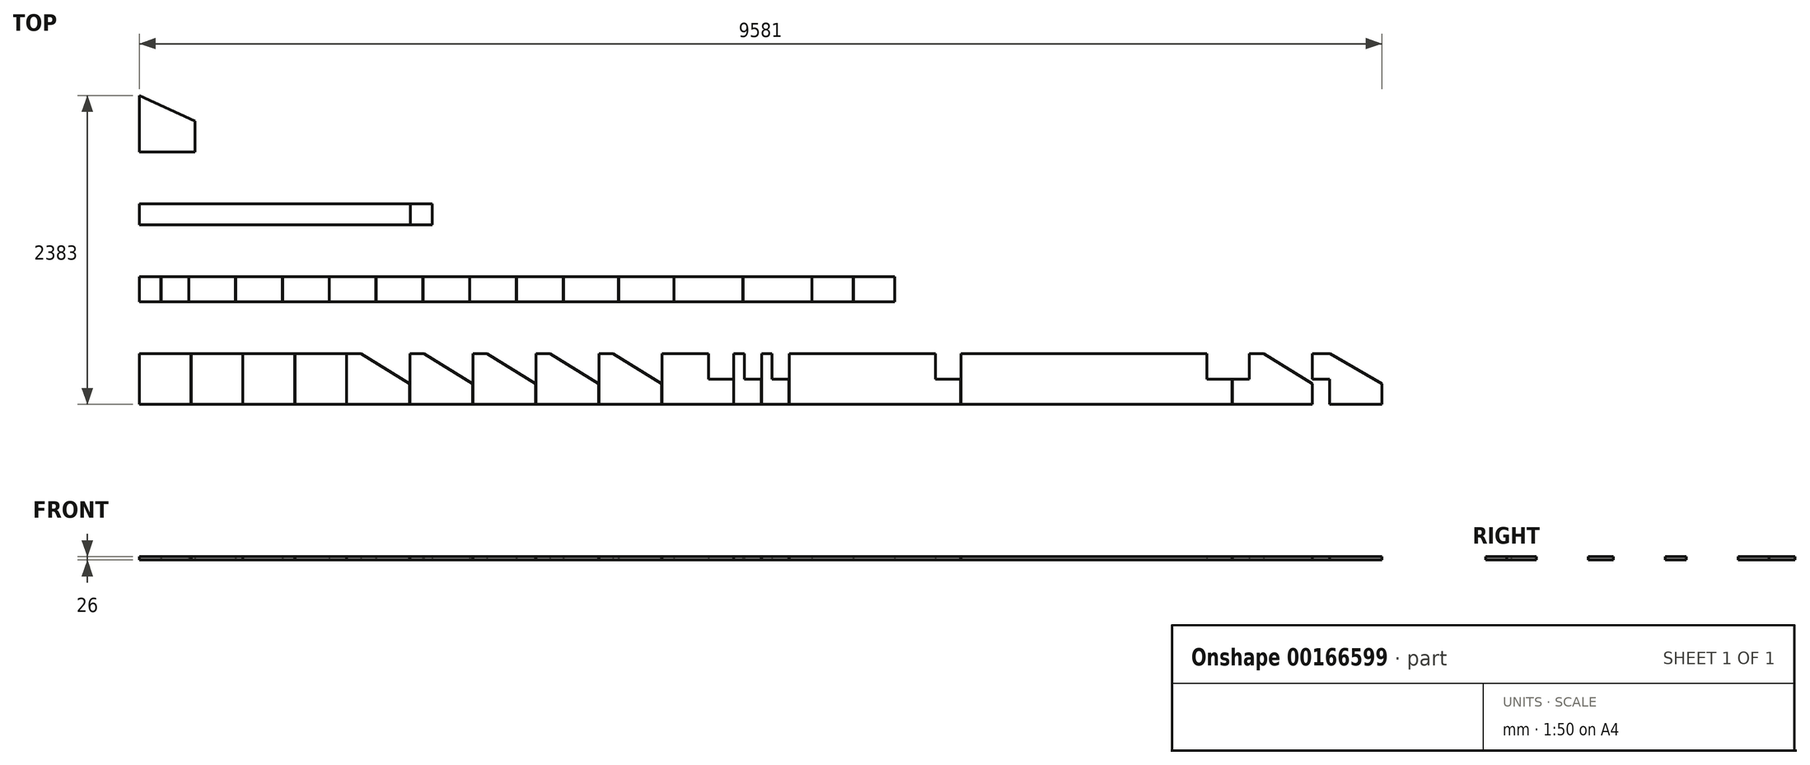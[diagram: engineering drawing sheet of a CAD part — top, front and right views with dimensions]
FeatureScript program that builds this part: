
annotation { "Feature Type Name" : "Feature", "Feature Type Description" : "" }
export const myFeature = defineFeature(function(context is Context, id is Id, definition is map)
    precondition{}
    {
        {
            var Q0;
            Q0=qCreatedBy(makeId("Top.planeOp"),FACE);
            var sketch = newSketch(context, id + "F0", { "sketchPlane" : qUnion([Q0])});
            skLineSegment(sketch, "E0.bottom", {"start": v(0, 0) * mm, "end": v(398, 0) * mm});
            skLineSegment(sketch, "E0.top", {"start": v(0, 390) * mm, "end": v(398, 390) * mm});
            skLineSegment(sketch, "E0.left", {"start": v(0, 0) * mm, "end": v(0, 390) * mm});
            skLineSegment(sketch, "E0.right", {"start": v(398, 0) * mm, "end": v(398, 390) * mm});
            skLineSegment(sketch, "E1.1.0.0", {"start": v(798, 0) * mm, "end": v(798, 390) * mm});
            skLineSegment(sketch, "E1.1.0.1", {"start": v(400, 0) * mm, "end": v(400, 390) * mm});
            skLineSegment(sketch, "E1.1.0.2", {"start": v(400, 390) * mm, "end": v(798, 390) * mm});
            skLineSegment(sketch, "E1.1.0.3", {"start": v(400, 0) * mm, "end": v(798, 0) * mm});
            skLineSegment(sketch, "E1.2.0.0", {"start": v(1198, 0) * mm, "end": v(1198, 390) * mm});
            skLineSegment(sketch, "E1.2.0.1", {"start": v(800, 0) * mm, "end": v(800, 390) * mm});
            skLineSegment(sketch, "E1.2.0.2", {"start": v(800, 390) * mm, "end": v(1198, 390) * mm});
            skLineSegment(sketch, "E1.2.0.3", {"start": v(800, 0) * mm, "end": v(1198, 0) * mm});
            skLineSegment(sketch, "E1.3.0.0", {"start": v(1598, 0) * mm, "end": v(1598, 390) * mm});
            skLineSegment(sketch, "E1.3.0.1", {"start": v(1200, 0) * mm, "end": v(1200, 390) * mm});
            skLineSegment(sketch, "E1.3.0.2", {"start": v(1200, 390) * mm, "end": v(1598, 390) * mm});
            skLineSegment(sketch, "E1.3.0.3", {"start": v(1200, 0) * mm, "end": v(1598, 0) * mm});
            skLineSegment(sketch, "E1.direction1", {"start": v(0, 0) * mm, "end": v(400, 0) * mm, "construction": true});
            skLineSegment(sketch, "E2.bottom", {"start": v(1600, 390) * mm, "end": v(1710, 390) * mm});
            skLineSegment(sketch, "E2.top", {"start": v(1600, 0) * mm, "end": v(2084, 0) * mm});
            skLineSegment(sketch, "E2.left", {"start": v(1600, 390) * mm, "end": v(1600, 0) * mm});
            skLineSegment(sketch, "E2.right", {"start": v(2084, 160) * mm, "end": v(2084, 0) * mm});
            skLineSegment(sketch, "E3", {"start": v(1710, 390) * mm, "end": v(2084, 160) * mm});
            skLineSegment(sketch, "E4.1.0.0", {"start": v(2086, 390) * mm, "end": v(2196, 390) * mm});
            skLineSegment(sketch, "E4.1.0.1", {"start": v(2196, 390) * mm, "end": v(2570, 160) * mm});
            skLineSegment(sketch, "E4.1.0.2", {"start": v(2086, 0) * mm, "end": v(2570, 0) * mm});
            skLineSegment(sketch, "E4.1.0.3", {"start": v(2570, 160) * mm, "end": v(2570, 0) * mm});
            skLineSegment(sketch, "E4.1.0.4", {"start": v(2086, 390) * mm, "end": v(2086, 0) * mm});
            skLineSegment(sketch, "E4.2.0.0", {"start": v(2572, 390) * mm, "end": v(2682, 390) * mm});
            skLineSegment(sketch, "E4.2.0.1", {"start": v(2682, 390) * mm, "end": v(3056, 160) * mm});
            skLineSegment(sketch, "E4.2.0.2", {"start": v(2572, 0) * mm, "end": v(3056, 0) * mm});
            skLineSegment(sketch, "E4.2.0.3", {"start": v(3056, 160) * mm, "end": v(3056, 0) * mm});
            skLineSegment(sketch, "E4.2.0.4", {"start": v(2572, 390) * mm, "end": v(2572, 0) * mm});
            skLineSegment(sketch, "E4.3.0.0", {"start": v(3058, 390) * mm, "end": v(3168, 390) * mm});
            skLineSegment(sketch, "E4.3.0.1", {"start": v(3168, 390) * mm, "end": v(3542, 160) * mm});
            skLineSegment(sketch, "E4.3.0.2", {"start": v(3058, 0) * mm, "end": v(3542, 0) * mm});
            skLineSegment(sketch, "E4.3.0.3", {"start": v(3542, 160) * mm, "end": v(3542, 0) * mm});
            skLineSegment(sketch, "E4.3.0.4", {"start": v(3058, 390) * mm, "end": v(3058, 0) * mm});
            skLineSegment(sketch, "E4.4.0.0", {"start": v(3544, 390) * mm, "end": v(3654, 390) * mm});
            skLineSegment(sketch, "E4.4.0.1", {"start": v(3654, 390) * mm, "end": v(4028, 160) * mm});
            skLineSegment(sketch, "E4.4.0.2", {"start": v(3544, 0) * mm, "end": v(4028, 0) * mm});
            skLineSegment(sketch, "E4.4.0.3", {"start": v(4028, 160) * mm, "end": v(4028, 0) * mm});
            skLineSegment(sketch, "E4.4.0.4", {"start": v(3544, 390) * mm, "end": v(3544, 0) * mm});
            skLineSegment(sketch, "E4.direction1", {"start": v(1600, 0) * mm, "end": v(2086, 0) * mm, "construction": true});
            skLineSegment(sketch, "E5.bottom", {"start": v(0, 790) * mm, "end": v(167, 790) * mm});
            skLineSegment(sketch, "E5.top", {"start": v(0, 985) * mm, "end": v(167, 985) * mm});
            skLineSegment(sketch, "E5.left", {"start": v(0, 790) * mm, "end": v(0, 985) * mm});
            skLineSegment(sketch, "E5.right", {"start": v(167, 790) * mm, "end": v(167, 985) * mm});
            skLineSegment(sketch, "E6.bottom", {"start": v(169, 790) * mm, "end": v(381, 790) * mm});
            skLineSegment(sketch, "E6.top", {"start": v(169, 985) * mm, "end": v(381, 985) * mm});
            skLineSegment(sketch, "E6.left", {"start": v(169, 790) * mm, "end": v(169, 985) * mm});
            skLineSegment(sketch, "E6.right", {"start": v(381, 790) * mm, "end": v(381, 985) * mm});
            skLineSegment(sketch, "E7.bottom", {"start": v(383, 790) * mm, "end": v(742, 790) * mm});
            skLineSegment(sketch, "E7.top", {"start": v(383, 985) * mm, "end": v(742, 985) * mm});
            skLineSegment(sketch, "E7.left", {"start": v(383, 790) * mm, "end": v(383, 985) * mm});
            skLineSegment(sketch, "E7.right", {"start": v(742, 790) * mm, "end": v(742, 985) * mm});
            skLineSegment(sketch, "E8.1.0.0", {"start": v(744, 985) * mm, "end": v(1103, 985) * mm});
            skLineSegment(sketch, "E8.1.0.1", {"start": v(744, 790) * mm, "end": v(744, 985) * mm});
            skLineSegment(sketch, "E8.1.0.2", {"start": v(744, 790) * mm, "end": v(1103, 790) * mm});
            skLineSegment(sketch, "E8.1.0.3", {"start": v(1103, 790) * mm, "end": v(1103, 985) * mm});
            skLineSegment(sketch, "E8.2.0.0", {"start": v(1105, 985) * mm, "end": v(1464, 985) * mm});
            skLineSegment(sketch, "E8.2.0.1", {"start": v(1105, 790) * mm, "end": v(1105, 985) * mm});
            skLineSegment(sketch, "E8.2.0.2", {"start": v(1105, 790) * mm, "end": v(1464, 790) * mm});
            skLineSegment(sketch, "E8.2.0.3", {"start": v(1464, 790) * mm, "end": v(1464, 985) * mm});
            skLineSegment(sketch, "E8.3.0.0", {"start": v(1466, 985) * mm, "end": v(1825, 985) * mm});
            skLineSegment(sketch, "E8.3.0.1", {"start": v(1466, 790) * mm, "end": v(1466, 985) * mm});
            skLineSegment(sketch, "E8.3.0.2", {"start": v(1466, 790) * mm, "end": v(1825, 790) * mm});
            skLineSegment(sketch, "E8.3.0.3", {"start": v(1825, 790) * mm, "end": v(1825, 985) * mm});
            skLineSegment(sketch, "E8.4.0.0", {"start": v(1827, 985) * mm, "end": v(2186, 985) * mm});
            skLineSegment(sketch, "E8.4.0.1", {"start": v(1827, 790) * mm, "end": v(1827, 985) * mm});
            skLineSegment(sketch, "E8.4.0.2", {"start": v(1827, 790) * mm, "end": v(2186, 790) * mm});
            skLineSegment(sketch, "E8.4.0.3", {"start": v(2186, 790) * mm, "end": v(2186, 985) * mm});
            skLineSegment(sketch, "E8.5.0.0", {"start": v(2188, 985) * mm, "end": v(2547, 985) * mm});
            skLineSegment(sketch, "E8.5.0.1", {"start": v(2188, 790) * mm, "end": v(2188, 985) * mm});
            skLineSegment(sketch, "E8.5.0.2", {"start": v(2188, 790) * mm, "end": v(2547, 790) * mm});
            skLineSegment(sketch, "E8.5.0.3", {"start": v(2547, 790) * mm, "end": v(2547, 985) * mm});
            skLineSegment(sketch, "E8.6.0.0", {"start": v(2549, 985) * mm, "end": v(2908, 985) * mm});
            skLineSegment(sketch, "E8.6.0.1", {"start": v(2549, 790) * mm, "end": v(2549, 985) * mm});
            skLineSegment(sketch, "E8.6.0.2", {"start": v(2549, 790) * mm, "end": v(2908, 790) * mm});
            skLineSegment(sketch, "E8.6.0.3", {"start": v(2908, 790) * mm, "end": v(2908, 985) * mm});
            skLineSegment(sketch, "E8.7.0.0", {"start": v(2910, 985) * mm, "end": v(3269, 985) * mm});
            skLineSegment(sketch, "E8.7.0.1", {"start": v(2910, 790) * mm, "end": v(2910, 985) * mm});
            skLineSegment(sketch, "E8.7.0.2", {"start": v(2910, 790) * mm, "end": v(3269, 790) * mm});
            skLineSegment(sketch, "E8.7.0.3", {"start": v(3269, 790) * mm, "end": v(3269, 985) * mm});
            skLineSegment(sketch, "E8.direction1", {"start": v(383, 790) * mm, "end": v(744, 790) * mm, "construction": true});
            skLineSegment(sketch, "E9.bottom", {"start": v(3271, 790) * mm, "end": v(3695, 790) * mm});
            skLineSegment(sketch, "E9.top", {"start": v(3271, 985) * mm, "end": v(3695, 985) * mm});
            skLineSegment(sketch, "E9.left", {"start": v(3271, 790) * mm, "end": v(3271, 985) * mm});
            skLineSegment(sketch, "E9.right", {"start": v(3695, 790) * mm, "end": v(3695, 985) * mm});
            skLineSegment(sketch, "E10.1.0.0", {"start": v(4121, 790) * mm, "end": v(4121, 985) * mm});
            skLineSegment(sketch, "E10.1.0.1", {"start": v(3697, 790) * mm, "end": v(3697, 985) * mm});
            skLineSegment(sketch, "E10.1.0.2", {"start": v(3697, 985) * mm, "end": v(4121, 985) * mm});
            skLineSegment(sketch, "E10.1.0.3", {"start": v(3697, 790) * mm, "end": v(4121, 790) * mm});
            skLineSegment(sketch, "E10.direction1", {"start": v(3271, 790) * mm, "end": v(3697, 790) * mm, "construction": true});
            skLineSegment(sketch, "E11.bottom", {"start": v(4123, 790) * mm, "end": v(4653, 790) * mm});
            skLineSegment(sketch, "E11.top", {"start": v(4123, 985) * mm, "end": v(4653, 985) * mm});
            skLineSegment(sketch, "E11.left", {"start": v(4123, 790) * mm, "end": v(4123, 985) * mm});
            skLineSegment(sketch, "E11.right", {"start": v(4653, 790) * mm, "end": v(4653, 985) * mm});
            skLineSegment(sketch, "E12.1.0.0", {"start": v(4655, 790) * mm, "end": v(4655, 985) * mm});
            skLineSegment(sketch, "E12.1.0.1", {"start": v(4655, 790) * mm, "end": v(5185, 790) * mm});
            skLineSegment(sketch, "E12.1.0.2", {"start": v(4655, 985) * mm, "end": v(5185, 985) * mm});
            skLineSegment(sketch, "E12.1.0.3", {"start": v(5185, 790) * mm, "end": v(5185, 985) * mm});
            skLineSegment(sketch, "E12.direction1", {"start": v(4123, 790) * mm, "end": v(4655, 790) * mm, "construction": true});
            skLineSegment(sketch, "E13.bottom", {"start": v(5187, 790) * mm, "end": v(5505, 790) * mm});
            skLineSegment(sketch, "E13.top", {"start": v(5187, 985) * mm, "end": v(5505, 985) * mm});
            skLineSegment(sketch, "E13.left", {"start": v(5187, 790) * mm, "end": v(5187, 985) * mm});
            skLineSegment(sketch, "E13.right", {"start": v(5505, 790) * mm, "end": v(5505, 985) * mm});
            skLineSegment(sketch, "E14.1.0.0", {"start": v(5507, 790) * mm, "end": v(5825, 790) * mm});
            skLineSegment(sketch, "E14.1.0.1", {"start": v(5507, 985) * mm, "end": v(5825, 985) * mm});
            skLineSegment(sketch, "E14.1.0.2", {"start": v(5507, 790) * mm, "end": v(5507, 985) * mm});
            skLineSegment(sketch, "E14.1.0.3", {"start": v(5825, 790) * mm, "end": v(5825, 985) * mm});
            skLineSegment(sketch, "E14.direction1", {"start": v(5187, 790) * mm, "end": v(5507, 790) * mm, "construction": true});
            skLineSegment(sketch, "E15.bottom", {"start": v(4030, 0) * mm, "end": v(4582, 0) * mm});
            skLineSegment(sketch, "E15.top", {"start": v(4030, 390) * mm, "end": v(4389, 390) * mm});
            skLineSegment(sketch, "E15.left", {"start": v(4030, 0) * mm, "end": v(4030, 390) * mm});
            skLineSegment(sketch, "E15.right", {"start": v(4582, 0) * mm, "end": v(4582, 195) * mm});
            skLineSegment(sketch, "E16", {"start": v(4389, 390) * mm, "end": v(4389, 195) * mm});
            skLineSegment(sketch, "E17", {"start": v(4389, 195) * mm, "end": v(4582, 195) * mm});
            skLineSegment(sketch, "E18.bottom", {"start": v(4584, 0) * mm, "end": v(4796, 0) * mm});
            skLineSegment(sketch, "E18.top", {"start": v(4584, 390) * mm, "end": v(4664, 390) * mm});
            skLineSegment(sketch, "E18.left", {"start": v(4584, 0) * mm, "end": v(4584, 390) * mm});
            skLineSegment(sketch, "E18.right", {"start": v(4796, 0) * mm, "end": v(4796, 195) * mm});
            skLineSegment(sketch, "E19", {"start": v(4664, 390) * mm, "end": v(4664, 195) * mm});
            skLineSegment(sketch, "E20", {"start": v(4664, 195) * mm, "end": v(4796, 195) * mm});
            skLineSegment(sketch, "E21.1.0.0", {"start": v(4798, 390) * mm, "end": v(4878, 390) * mm});
            skLineSegment(sketch, "E21.1.0.1", {"start": v(4798, 0) * mm, "end": v(5010, 0) * mm});
            skLineSegment(sketch, "E21.1.0.2", {"start": v(4878, 390) * mm, "end": v(4878, 195) * mm});
            skLineSegment(sketch, "E21.1.0.3", {"start": v(5010, 0) * mm, "end": v(5010, 195) * mm});
            skLineSegment(sketch, "E21.1.0.4", {"start": v(4798, 0) * mm, "end": v(4798, 390) * mm});
            skLineSegment(sketch, "E21.1.0.5", {"start": v(4878, 195) * mm, "end": v(5010, 195) * mm});
            skLineSegment(sketch, "E21.direction1", {"start": v(4584, 0) * mm, "end": v(4798, 0) * mm, "construction": true});
            skLineSegment(sketch, "E22.bottom", {"start": v(5012, 0) * mm, "end": v(6333, 0) * mm});
            skLineSegment(sketch, "E22.top", {"start": v(5012, 390) * mm, "end": v(6140, 390) * mm});
            skLineSegment(sketch, "E22.left", {"start": v(5012, 0) * mm, "end": v(5012, 390) * mm});
            skLineSegment(sketch, "E22.right", {"start": v(6333, 0) * mm, "end": v(6333, 195) * mm});
            skLineSegment(sketch, "E23", {"start": v(6140, 390) * mm, "end": v(6140, 195) * mm});
            skLineSegment(sketch, "E24", {"start": v(6140, 195) * mm, "end": v(6333, 195) * mm});
            skLineSegment(sketch, "E25.bottom", {"start": v(6335, 0) * mm, "end": v(8425, 0) * mm});
            skLineSegment(sketch, "E25.top", {"start": v(6335, 390) * mm, "end": v(8232, 390) * mm});
            skLineSegment(sketch, "E25.left", {"start": v(6335, 0) * mm, "end": v(6335, 390) * mm});
            skLineSegment(sketch, "E25.right", {"start": v(8425, 0) * mm, "end": v(8425, 195) * mm});
            skLineSegment(sketch, "E26", {"start": v(8232, 390) * mm, "end": v(8232, 195) * mm});
            skLineSegment(sketch, "E27", {"start": v(8232, 195) * mm, "end": v(8425, 195) * mm});
            skLineSegment(sketch, "E28.bottom", {"start": v(0, 1385) * mm, "end": v(2090, 1385) * mm});
            skLineSegment(sketch, "E28.top", {"start": v(0, 1545) * mm, "end": v(2090, 1545) * mm});
            skLineSegment(sketch, "E28.left", {"start": v(0, 1385) * mm, "end": v(0, 1545) * mm});
            skLineSegment(sketch, "E28.right", {"start": v(2090, 1385) * mm, "end": v(2090, 1545) * mm});
            skLineSegment(sketch, "E29.bottom", {"start": v(8427, 0) * mm, "end": v(9043, 0) * mm});
            skLineSegment(sketch, "E29.top", {"start": v(8559, 390) * mm, "end": v(8669, 390) * mm});
            skLineSegment(sketch, "E29.left", {"start": v(8427, 0) * mm, "end": v(8427, 195) * mm});
            skLineSegment(sketch, "E29.right", {"start": v(9043, 0) * mm, "end": v(9043, 160) * mm});
            skLineSegment(sketch, "E30", {"start": v(8559, 390) * mm, "end": v(8559, 195) * mm});
            skLineSegment(sketch, "E31", {"start": v(8559, 195) * mm, "end": v(8427, 195) * mm});
            skLineSegment(sketch, "E32", {"start": v(8669, 390) * mm, "end": v(9043, 160) * mm});
            skLineSegment(sketch, "E33.bottom", {"start": v(9177, 0) * mm, "end": v(9581, 0) * mm});
            skLineSegment(sketch, "E33.top", {"start": v(9045, 390) * mm, "end": v(9181, 390) * mm});
            skLineSegment(sketch, "E33.left", {"start": v(9045, 195) * mm, "end": v(9045, 390) * mm});
            skLineSegment(sketch, "E33.right", {"start": v(9581, 0) * mm, "end": v(9581, 160) * mm});
            skLineSegment(sketch, "E34", {"start": v(9177, 0) * mm, "end": v(9177, 195) * mm});
            skLineSegment(sketch, "E35", {"start": v(9177, 195) * mm, "end": v(9045, 195) * mm});
            skLineSegment(sketch, "E36", {"start": v(9181, 390) * mm, "end": v(9581, 160) * mm});
            skLineSegment(sketch, "E37.bottom", {"start": v(0, 1945) * mm, "end": v(430, 1945) * mm});
            skLineSegment(sketch, "E37.left", {"start": v(0, 1945) * mm, "end": v(0, 2383) * mm});
            skLineSegment(sketch, "E37.right", {"start": v(430, 1945) * mm, "end": v(430, 2184) * mm});
            skLineSegment(sketch, "E38", {"start": v(0, 2383) * mm, "end": v(430, 2184) * mm});
            skLineSegment(sketch, "E39.bottom", {"start": v(2092, 1545) * mm, "end": v(2259, 1545) * mm});
            skLineSegment(sketch, "E39.top", {"start": v(2092, 1385) * mm, "end": v(2259, 1385) * mm});
            skLineSegment(sketch, "E39.left", {"start": v(2092, 1545) * mm, "end": v(2092, 1385) * mm});
            skLineSegment(sketch, "E39.right", {"start": v(2259, 1545) * mm, "end": v(2259, 1385) * mm});
            skLineSegment(sketch, "E40.bottom", {"start": v(0, -315.86) * mm, "end": v(2200, -315.86) * mm});
            skLineSegment(sketch, "E40.top", {"start": v(0, -905.86) * mm, "end": v(2200, -905.86) * mm});
            skLineSegment(sketch, "E40.left", {"start": v(0, -315.86) * mm, "end": v(0, -905.86) * mm});
            skLineSegment(sketch, "E40.right", {"start": v(2200, -315.86) * mm, "end": v(2200, -905.86) * mm});
            skLineSegment(sketch, "E41.1.0.0", {"start": v(2250, -905.86) * mm, "end": v(4450, -905.86) * mm});
            skLineSegment(sketch, "E41.1.0.1", {"start": v(4450, -315.86) * mm, "end": v(4450, -905.86) * mm});
            skLineSegment(sketch, "E41.1.0.2", {"start": v(2250, -315.86) * mm, "end": v(2250, -905.86) * mm});
            skLineSegment(sketch, "E41.1.0.3", {"start": v(2250, -315.86) * mm, "end": v(4450, -315.86) * mm});
            skLineSegment(sketch, "E41.2.0.0", {"start": v(4500, -905.86) * mm, "end": v(6700, -905.86) * mm});
            skLineSegment(sketch, "E41.2.0.1", {"start": v(6700, -315.86) * mm, "end": v(6700, -905.86) * mm});
            skLineSegment(sketch, "E41.2.0.2", {"start": v(4500, -315.86) * mm, "end": v(4500, -905.86) * mm});
            skLineSegment(sketch, "E41.2.0.3", {"start": v(4500, -315.86) * mm, "end": v(6700, -315.86) * mm});
            skLineSegment(sketch, "E41.3.0.0", {"start": v(6750, -905.86) * mm, "end": v(8950, -905.86) * mm});
            skLineSegment(sketch, "E41.3.0.1", {"start": v(8950, -315.86) * mm, "end": v(8950, -905.86) * mm});
            skLineSegment(sketch, "E41.3.0.2", {"start": v(6750, -315.86) * mm, "end": v(6750, -905.86) * mm});
            skLineSegment(sketch, "E41.3.0.3", {"start": v(6750, -315.86) * mm, "end": v(8950, -315.86) * mm});
            skLineSegment(sketch, "E41.4.0.0", {"start": v(9000, -905.86) * mm, "end": v(11200, -905.86) * mm});
            skLineSegment(sketch, "E41.4.0.1", {"start": v(11200, -315.86) * mm, "end": v(11200, -905.86) * mm});
            skLineSegment(sketch, "E41.4.0.2", {"start": v(9000, -315.86) * mm, "end": v(9000, -905.86) * mm});
            skLineSegment(sketch, "E41.4.0.3", {"start": v(9000, -315.86) * mm, "end": v(11200, -315.86) * mm});
            skLineSegment(sketch, "E41.direction1", {"start": v(0, -905.86) * mm, "end": v(2250, -905.86) * mm, "construction": true});
            skLineSegment(sketch, "E42", {"start": v(3269, 790) * mm, "end": v(3271, 790) * mm, "construction": true});
            skSolve(sketch);
        }
        {
            var Q0;
            Q0=makeQuery(id+"F0.imprint","IMPRINT",FACE,{"disambiguationData":[TD([[makeQuery(id+"F0.imprint","IMPRINT",EDGE,{"derivedFrom":sQuery(id+"F0.wireOp",EDGE,"E0.bottom")}),1.0]])]});
            var Q1;
            Q1=makeQuery(id+"F0.imprint","IMPRINT",FACE,{"disambiguationData":[TD([[makeQuery(id+"F0.imprint","IMPRINT",EDGE,{"derivedFrom":sQuery(id+"F0.wireOp",EDGE,"E1.1.0.0")}),1.0]])]});
            var Q2;
            Q2=makeQuery(id+"F0.imprint","IMPRINT",FACE,{"disambiguationData":[TD([[makeQuery(id+"F0.imprint","IMPRINT",EDGE,{"derivedFrom":sQuery(id+"F0.wireOp",EDGE,"E1.2.0.0")}),1.0]])]});
            var Q3;
            Q3=makeQuery(id+"F0.imprint","IMPRINT",FACE,{"disambiguationData":[TD([[makeQuery(id+"F0.imprint","IMPRINT",EDGE,{"derivedFrom":sQuery(id+"F0.wireOp",EDGE,"E1.3.0.0")}),1.0]])]});
            var Q4;
            Q4=makeQuery(id+"F0.imprint","IMPRINT",FACE,{"disambiguationData":[TD([[makeQuery(id+"F0.imprint","IMPRINT",EDGE,{"derivedFrom":sQuery(id+"F0.wireOp",EDGE,"E2.bottom")}),-1.0]])]});
            var Q5;
            Q5=makeQuery(id+"F0.imprint","IMPRINT",FACE,{"disambiguationData":[TD([[makeQuery(id+"F0.imprint","IMPRINT",EDGE,{"derivedFrom":sQuery(id+"F0.wireOp",EDGE,"E4.1.0.0")}),-1.0]])]});
            var Q6;
            Q6=makeQuery(id+"F0.imprint","IMPRINT",FACE,{"disambiguationData":[TD([[makeQuery(id+"F0.imprint","IMPRINT",EDGE,{"derivedFrom":sQuery(id+"F0.wireOp",EDGE,"E4.2.0.0")}),-1.0]])]});
            var Q7;
            Q7=makeQuery(id+"F0.imprint","IMPRINT",FACE,{"disambiguationData":[TD([[makeQuery(id+"F0.imprint","IMPRINT",EDGE,{"derivedFrom":sQuery(id+"F0.wireOp",EDGE,"E4.3.0.0")}),-1.0]])]});
            var Q8;
            Q8=makeQuery(id+"F0.imprint","IMPRINT",FACE,{"disambiguationData":[TD([[makeQuery(id+"F0.imprint","IMPRINT",EDGE,{"derivedFrom":sQuery(id+"F0.wireOp",EDGE,"E4.4.0.0")}),-1.0]])]});
            var Q9;
            Q9=makeQuery(id+"F0.imprint","IMPRINT",FACE,{"disambiguationData":[TD([[makeQuery(id+"F0.imprint","IMPRINT",EDGE,{"derivedFrom":sQuery(id+"F0.wireOp",EDGE,"E5.bottom")}),1.0]])]});
            var Q10;
            Q10=makeQuery(id+"F0.imprint","IMPRINT",FACE,{"disambiguationData":[TD([[makeQuery(id+"F0.imprint","IMPRINT",EDGE,{"derivedFrom":sQuery(id+"F0.wireOp",EDGE,"E6.bottom")}),1.0]])]});
            var Q11;
            Q11=makeQuery(id+"F0.imprint","IMPRINT",FACE,{"disambiguationData":[TD([[makeQuery(id+"F0.imprint","IMPRINT",EDGE,{"derivedFrom":sQuery(id+"F0.wireOp",EDGE,"E7.bottom")}),1.0]])]});
            var Q12;
            Q12=makeQuery(id+"F0.imprint","IMPRINT",FACE,{"disambiguationData":[TD([[makeQuery(id+"F0.imprint","IMPRINT",EDGE,{"derivedFrom":sQuery(id+"F0.wireOp",EDGE,"E8.1.0.0")}),-1.0]])]});
            var Q13;
            Q13=makeQuery(id+"F0.imprint","IMPRINT",FACE,{"disambiguationData":[TD([[makeQuery(id+"F0.imprint","IMPRINT",EDGE,{"derivedFrom":sQuery(id+"F0.wireOp",EDGE,"E8.2.0.0")}),-1.0]])]});
            var Q14;
            Q14=makeQuery(id+"F0.imprint","IMPRINT",FACE,{"disambiguationData":[TD([[makeQuery(id+"F0.imprint","IMPRINT",EDGE,{"derivedFrom":sQuery(id+"F0.wireOp",EDGE,"E8.3.0.0")}),-1.0]])]});
            var Q15;
            Q15=makeQuery(id+"F0.imprint","IMPRINT",FACE,{"disambiguationData":[TD([[makeQuery(id+"F0.imprint","IMPRINT",EDGE,{"derivedFrom":sQuery(id+"F0.wireOp",EDGE,"E8.4.0.0")}),-1.0]])]});
            var Q16;
            Q16=makeQuery(id+"F0.imprint","IMPRINT",FACE,{"disambiguationData":[TD([[makeQuery(id+"F0.imprint","IMPRINT",EDGE,{"derivedFrom":sQuery(id+"F0.wireOp",EDGE,"E8.5.0.0")}),-1.0]])]});
            var Q17;
            Q17=makeQuery(id+"F0.imprint","IMPRINT",FACE,{"disambiguationData":[TD([[makeQuery(id+"F0.imprint","IMPRINT",EDGE,{"derivedFrom":sQuery(id+"F0.wireOp",EDGE,"E8.6.0.0")}),-1.0]])]});
            var Q18;
            Q18=makeQuery(id+"F0.imprint","IMPRINT",FACE,{"disambiguationData":[TD([[makeQuery(id+"F0.imprint","IMPRINT",EDGE,{"derivedFrom":sQuery(id+"F0.wireOp",EDGE,"E8.7.0.0")}),-1.0]])]});
            var Q19;
            Q19=makeQuery(id+"F0.imprint","IMPRINT",FACE,{"disambiguationData":[TD([[makeQuery(id+"F0.imprint","IMPRINT",EDGE,{"derivedFrom":sQuery(id+"F0.wireOp",EDGE,"E9.bottom")}),1.0]])]});
            var Q20;
            Q20=makeQuery(id+"F0.imprint","IMPRINT",FACE,{"disambiguationData":[TD([[makeQuery(id+"F0.imprint","IMPRINT",EDGE,{"derivedFrom":sQuery(id+"F0.wireOp",EDGE,"E10.1.0.0")}),1.0]])]});
            var Q21;
            Q21=makeQuery(id+"F0.imprint","IMPRINT",FACE,{"disambiguationData":[TD([[makeQuery(id+"F0.imprint","IMPRINT",EDGE,{"derivedFrom":sQuery(id+"F0.wireOp",EDGE,"E11.bottom")}),1.0]])]});
            var Q22;
            Q22=makeQuery(id+"F0.imprint","IMPRINT",FACE,{"disambiguationData":[TD([[makeQuery(id+"F0.imprint","IMPRINT",EDGE,{"derivedFrom":sQuery(id+"F0.wireOp",EDGE,"E12.1.0.0")}),-1.0]])]});
            var Q23;
            Q23=makeQuery(id+"F0.imprint","IMPRINT",FACE,{"disambiguationData":[TD([[makeQuery(id+"F0.imprint","IMPRINT",EDGE,{"derivedFrom":sQuery(id+"F0.wireOp",EDGE,"E13.bottom")}),1.0]])]});
            var Q24;
            Q24=makeQuery(id+"F0.imprint","IMPRINT",FACE,{"disambiguationData":[TD([[makeQuery(id+"F0.imprint","IMPRINT",EDGE,{"derivedFrom":sQuery(id+"F0.wireOp",EDGE,"E14.1.0.0")}),1.0]])]});
            var Q25;
            Q25=makeQuery(id+"F0.imprint","IMPRINT",FACE,{"disambiguationData":[TD([[makeQuery(id+"F0.imprint","IMPRINT",EDGE,{"derivedFrom":sQuery(id+"F0.wireOp",EDGE,"E15.bottom")}),1.0]])]});
            var Q26;
            Q26=makeQuery(id+"F0.imprint","IMPRINT",FACE,{"disambiguationData":[TD([[makeQuery(id+"F0.imprint","IMPRINT",EDGE,{"derivedFrom":sQuery(id+"F0.wireOp",EDGE,"E18.bottom")}),1.0]])]});
            var Q27;
            Q27=makeQuery(id+"F0.imprint","IMPRINT",FACE,{"disambiguationData":[TD([[makeQuery(id+"F0.imprint","IMPRINT",EDGE,{"derivedFrom":sQuery(id+"F0.wireOp",EDGE,"E21.1.0.0")}),-1.0]])]});
            var Q28;
            Q28=makeQuery(id+"F0.imprint","IMPRINT",FACE,{"disambiguationData":[TD([[makeQuery(id+"F0.imprint","IMPRINT",EDGE,{"derivedFrom":sQuery(id+"F0.wireOp",EDGE,"E22.bottom")}),1.0]])]});
            var Q29;
            Q29=makeQuery(id+"F0.imprint","IMPRINT",FACE,{"disambiguationData":[TD([[makeQuery(id+"F0.imprint","IMPRINT",EDGE,{"derivedFrom":sQuery(id+"F0.wireOp",EDGE,"E25.bottom")}),1.0]])]});
            var Q30;
            Q30=makeQuery(id+"F0.imprint","IMPRINT",FACE,{"disambiguationData":[TD([[makeQuery(id+"F0.imprint","IMPRINT",EDGE,{"derivedFrom":sQuery(id+"F0.wireOp",EDGE,"E28.bottom")}),1.0]])]});
            var Q31;
            Q31=makeQuery(id+"F0.imprint","IMPRINT",FACE,{"disambiguationData":[TD([[makeQuery(id+"F0.imprint","IMPRINT",EDGE,{"derivedFrom":sQuery(id+"F0.wireOp",EDGE,"E29.bottom")}),1.0]])]});
            var Q32;
            Q32=makeQuery(id+"F0.imprint","IMPRINT",FACE,{"disambiguationData":[TD([[makeQuery(id+"F0.imprint","IMPRINT",EDGE,{"derivedFrom":sQuery(id+"F0.wireOp",EDGE,"E33.bottom")}),1.0]])]});
            var Q33;
            Q33=makeQuery(id+"F0.imprint","IMPRINT",FACE,{"disambiguationData":[TD([[makeQuery(id+"F0.imprint","IMPRINT",EDGE,{"derivedFrom":sQuery(id+"F0.wireOp",EDGE,"E37.bottom")}),1.0]])]});
            var Q34;
            Q34=makeQuery(id+"F0.imprint","IMPRINT",FACE,{"disambiguationData":[TD([[makeQuery(id+"F0.imprint","IMPRINT",EDGE,{"derivedFrom":sQuery(id+"F0.wireOp",EDGE,"E39.bottom")}),-1.0]])]});
            extrude(context, id + "F1", {"entities" : qUnion([Q0, Q1, Q2, Q3, Q4, Q5, Q6, Q7, Q8, Q9, Q10, Q11, Q12, Q13, Q14, Q15, Q16, Q17, Q18, Q19, Q20, Q21, Q22, Q23, Q24, Q25, Q26, Q27, Q28, Q29, Q30, Q31, Q32, Q33, Q34]), "depth" : 26 * mm});
        }
    });
